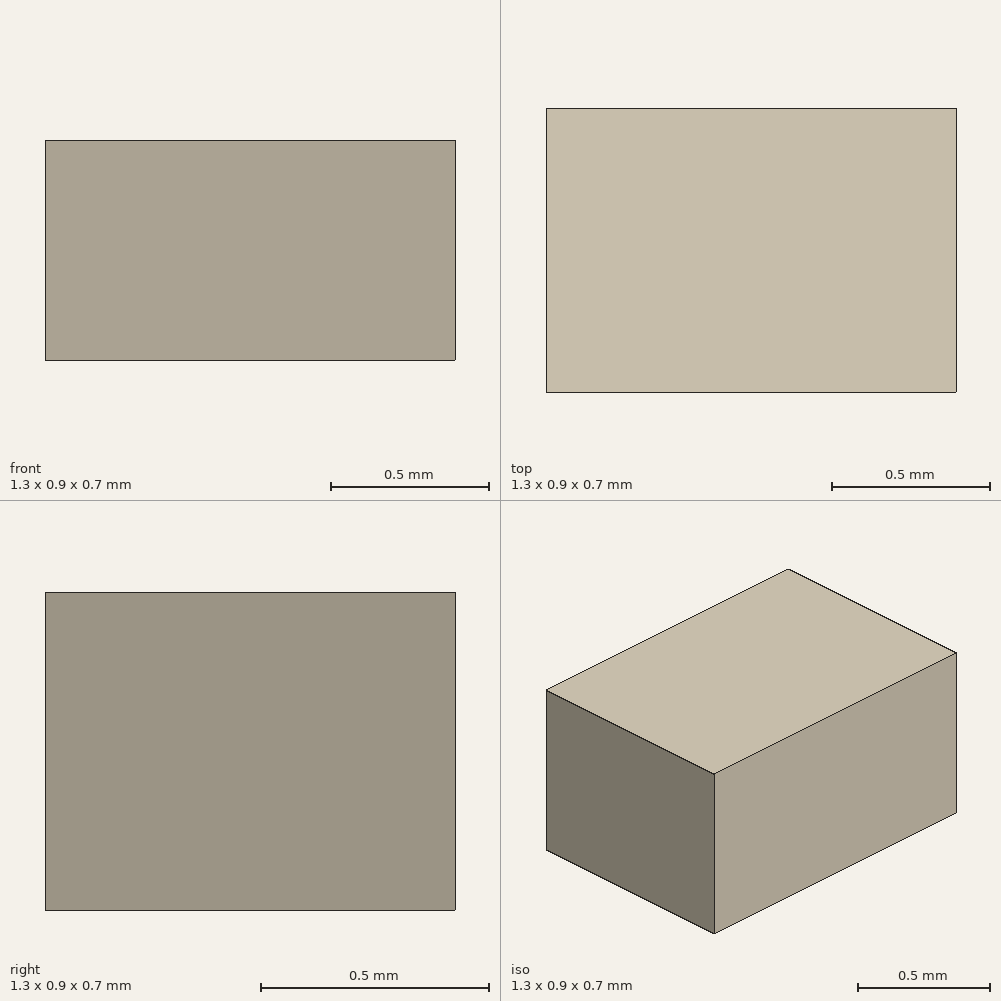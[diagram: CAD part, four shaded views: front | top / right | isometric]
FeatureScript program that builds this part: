
annotation { "Feature Type Name" : "Feature", "Feature Type Description" : "" }
export const myFeature = defineFeature(function(context is Context, id is Id, definition is map)
    precondition{}
    {
        {
            var Q0;
            Q0=qCreatedBy(makeId("Top.planeOp"),FACE);
            var sketch = newSketch(context, id + "F0", { "sketchPlane" : qUnion([Q0])});
            skLineSegment(sketch, "E0.bottom", {"start": v(0.2, 1.05) * mm, "end": v(1.5, 1.05) * mm});
            skLineSegment(sketch, "E0.top", {"start": v(0.2, 0.15) * mm, "end": v(1.5, 0.15) * mm});
            skLineSegment(sketch, "E0.left", {"start": v(0.2, 1.05) * mm, "end": v(0.2, 0.15) * mm});
            skLineSegment(sketch, "E0.right", {"start": v(1.5, 1.05) * mm, "end": v(1.5, 0.15) * mm});
            skSolve(sketch);
        }
        {
            var Q0;
            Q0=makeQuery(id+"F0.imprint","IMPRINT",FACE,{"disambiguationData":[TD([[makeQuery(id+"F0.imprint","IMPRINT",EDGE,{"derivedFrom":sQuery(id+"F0.wireOp",EDGE,"E0.bottom")}),-1.0]])]});
            extrude(context, id + "F1", {"entities" : qUnion([Q0]), "depth" : .7 * mm});
        }
    });
